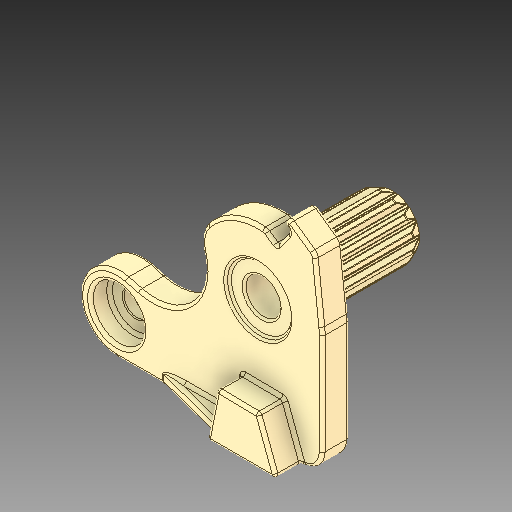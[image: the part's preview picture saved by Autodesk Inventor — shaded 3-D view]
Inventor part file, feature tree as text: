
AUTODESK INVENTOR PART (.ipt)
format: ipt  version: 2019 (Build 230136000, 136)  size: 1,862,656 bytes
history: native  units: in
note: dims shown in document units (in); Inventor stores cm internally (conversion verified against a paired STEP export)
features: sketch x12, other x3
ambient origin geometry x8: Origin, YZ Plane, XZ Plane, XY Plane, X Axis, Y Axis, Z Axis, Center Point
bodies: Solid1 (feature_tree)
feature tree (15):
  other  "Bell Crank Side Handle.ipt"
  other  "Solid1::Bell Crank Side Handle.ipt"
  other  "TaggingFeature1"
  sketch  "Sketch1"  dims[d0=0.3937in]
  sketch  "Sketch2"
  sketch  "Sketch3"
  sketch  "Sketch7"
  sketch  "Sketch8"
  sketch  "Sketch9"
  sketch  "Sketch10"
  sketch  "Sketch11"
  sketch  "Sketch12"
  sketch  "Sketch13"
  sketch  "Sketch15"
  sketch  "Sketch16"
